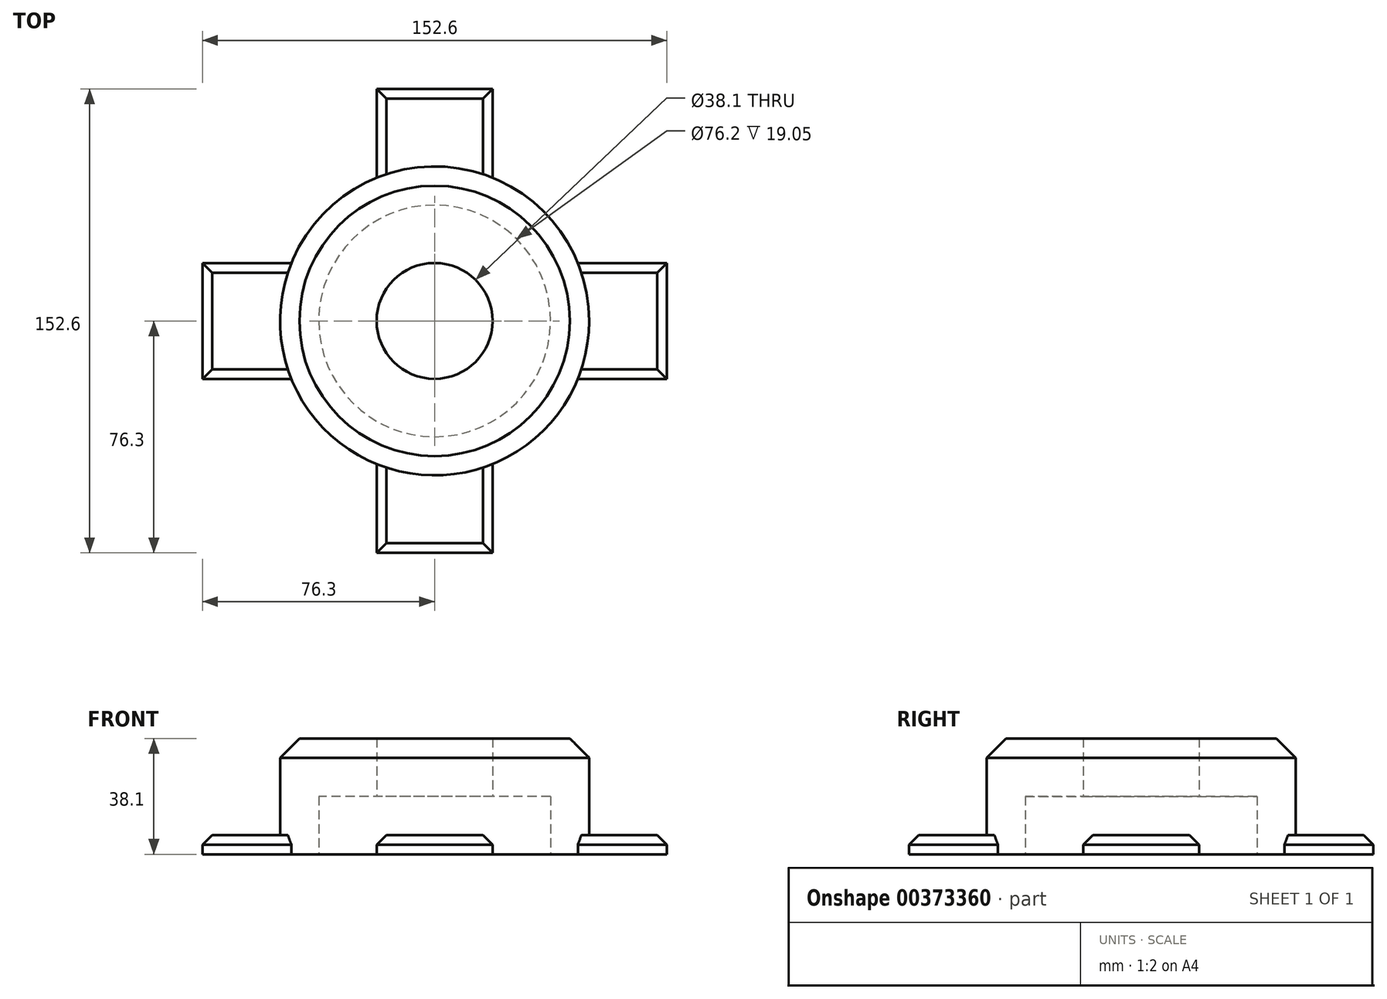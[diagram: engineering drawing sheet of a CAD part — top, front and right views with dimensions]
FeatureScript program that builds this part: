
annotation { "Feature Type Name" : "Feature", "Feature Type Description" : "" }
export const myFeature = defineFeature(function(context is Context, id is Id, definition is map)
    precondition{}
    {
        {
            var Q0;
            Q0=qCreatedBy(makeId("Top.planeOp"),FACE);
            var sketch = newSketch(context, id + "F0", { "sketchPlane" : qUnion([Q0])});
            skCircle(sketch, "E0", {"center": v(0, 0) * mm, "radius": 50.8 * mm});
            skLineSegment(sketch, "E1", {"start": v(0, 75.73) * mm, "end": v(0, -75.72) * mm, "construction": true});
            skLineSegment(sketch, "E2", {"start": v(-75.97, 0) * mm, "end": v(76.3, 0) * mm, "construction": true});
            skLineSegment(sketch, "E3", {"start": v(-19.05, 47.1) * mm, "end": v(-19.05, 76.3) * mm});
            skLineSegment(sketch, "E4", {"start": v(19.05, 47.1) * mm, "end": v(19.05, 76.3) * mm});
            skLineSegment(sketch, "E5", {"start": v(-47.1, 19.05) * mm, "end": v(-76.3, 19.05) * mm});
            skLineSegment(sketch, "E6", {"start": v(-47.1, -19.05) * mm, "end": v(-76.3, -19.05) * mm});
            skLineSegment(sketch, "E7", {"start": v(47.1, 19.05) * mm, "end": v(76.3, 19.05) * mm});
            skLineSegment(sketch, "E8", {"start": v(47.1, -19.05) * mm, "end": v(76.3, -19.05) * mm});
            skLineSegment(sketch, "E9", {"start": v(-19.05, -47.1) * mm, "end": v(-19.05, -76.3) * mm});
            skLineSegment(sketch, "E10", {"start": v(19.05, -47.1) * mm, "end": v(19.05, -76.3) * mm});
            skLineSegment(sketch, "E11", {"start": v(-76.3, 19.05) * mm, "end": v(-76.3, -19.05) * mm});
            skLineSegment(sketch, "E12", {"start": v(-19.05, 76.3) * mm, "end": v(19.05, 76.3) * mm});
            skLineSegment(sketch, "E13", {"start": v(76.3, 19.05) * mm, "end": v(76.3, -19.05) * mm});
            skLineSegment(sketch, "E14", {"start": v(19.05, -76.3) * mm, "end": v(-19.05, -76.3) * mm});
            skCircle(sketch, "E15", {"center": v(0, 0) * mm, "radius": 19.05 * mm});
            skSolve(sketch);
        }
        {
            var Q0;
            {var subQ0=sQuery(id+"F0.wireOp",EDGE,"E0");var subQ4=makeQuery(id+"F0.imprint","INTERSECT",VERTEX,{"derivedFrom":[subQ0,sQuery(id+"F0.wireOp",EDGE,"E4")]});Q0=makeQuery(id+"F0.imprint","IMPRINT",FACE,{"disambiguationData":[TD([[makeQuery(id+"F0.imprint","IMPRINT",EDGE,{"disambiguationData":[TD([[subQ4,1.0]])],"derivedFrom":subQ0}),1.0]])]});}
            extrude(context, id + "F1", {"entities" : qUnion([Q0]), "depth" : 38.1 * mm});
        }
        {
            var Q0;
            {var subQ0=sQuery(id+"F0.wireOp",EDGE,"E9");Q0=makeQuery(id+"F0.imprint","IMPRINT",FACE,{"disambiguationData":[TD([[makeQuery(id+"F0.imprint","IMPRINT",EDGE,{"derivedFrom":subQ0}),1.0]])]});}
            var Q1;
            {var subQ0=sQuery(id+"F0.wireOp",EDGE,"E5");Q1=makeQuery(id+"F0.imprint","IMPRINT",FACE,{"disambiguationData":[TD([[makeQuery(id+"F0.imprint","IMPRINT",EDGE,{"derivedFrom":subQ0}),1.0]])]});}
            var Q2;
            {var subQ0=sQuery(id+"F0.wireOp",EDGE,"E7");Q2=makeQuery(id+"F0.imprint","IMPRINT",FACE,{"disambiguationData":[TD([[makeQuery(id+"F0.imprint","IMPRINT",EDGE,{"derivedFrom":subQ0}),-1.0]])]});}
            var Q3;
            {var subQ0=sQuery(id+"F0.wireOp",EDGE,"E3");Q3=makeQuery(id+"F0.imprint","IMPRINT",FACE,{"disambiguationData":[TD([[makeQuery(id+"F0.imprint","IMPRINT",EDGE,{"derivedFrom":subQ0}),-1.0]])]});}
            extrude(context, id + "F2", {"entities" : qUnion([Q0, Q1, Q2, Q3]), "operationType" : NewBodyOperationType.ADD, "depth" : 6.35 * mm});
        }
        {
            var Q0;
            Q0=makeQuery(id+"F0.imprint","IMPRINT",FACE,{"disambiguationData":[TD([[makeQuery(id+"F0.imprint","IMPRINT",EDGE,{"derivedFrom":sQuery(id+"F0.wireOp",EDGE,"E15")}),-1.0]])]});
            var sketch = newSketch(context, id + "F3", { "sketchPlane" : qUnion([Q0])});
            skCircle(sketch, "E16", {"center": v(0, 0) * mm, "radius": 38.1 * mm});
            skSolve(sketch);
        }
        {
            var Q0;
            Q0 = qSketchRegion(id + "F3", true);
            extrude(context, id + "F4", {"entities" : qUnion([Q0]), "operationType" : NewBodyOperationType.REMOVE, "depth" : 19.05 * mm});
        }
        {
            var Q0;
            Q0=makeQuery(id+"F2.opExtrude","CAP_EDGE",EDGE,{"disambiguationData":[OSD([sQuery(id+"F0.wireOp",EDGE,"E14")])],"isStart":false});
            var Q1;
            Q1=makeQuery(id+"F2.opExtrude","CAP_EDGE",EDGE,{"disambiguationData":[OSD([sQuery(id+"F0.wireOp",EDGE,"E10")])],"isStart":false});
            var Q2;
            Q2=makeQuery(id+"F2.opExtrude","CAP_EDGE",EDGE,{"disambiguationData":[OSD([sQuery(id+"F0.wireOp",EDGE,"E9")])],"isStart":false});
            var Q3;
            Q3=makeQuery(id+"F2.opExtrude","CAP_EDGE",EDGE,{"disambiguationData":[OSD([sQuery(id+"F0.wireOp",EDGE,"E8")])],"isStart":false});
            var Q4;
            Q4=makeQuery(id+"F2.opExtrude","CAP_EDGE",EDGE,{"disambiguationData":[OSD([sQuery(id+"F0.wireOp",EDGE,"E13")])],"isStart":false});
            var Q5;
            Q5=makeQuery(id+"F2.opExtrude","CAP_EDGE",EDGE,{"disambiguationData":[OSD([sQuery(id+"F0.wireOp",EDGE,"E7")])],"isStart":false});
            var Q6;
            Q6=makeQuery(id+"F2.opExtrude","CAP_EDGE",EDGE,{"disambiguationData":[OSD([sQuery(id+"F0.wireOp",EDGE,"E5")])],"isStart":false});
            var Q7;
            Q7=makeQuery(id+"F2.opExtrude","CAP_EDGE",EDGE,{"disambiguationData":[OSD([sQuery(id+"F0.wireOp",EDGE,"E11")])],"isStart":false});
            var Q8;
            Q8=makeQuery(id+"F2.opExtrude","CAP_EDGE",EDGE,{"disambiguationData":[OSD([sQuery(id+"F0.wireOp",EDGE,"E6")])],"isStart":false});
            var Q9;
            Q9=makeQuery(id+"F2.opExtrude","CAP_EDGE",EDGE,{"disambiguationData":[OSD([sQuery(id+"F0.wireOp",EDGE,"E12")])],"isStart":false});
            var Q10;
            Q10=makeQuery(id+"F2.opExtrude","CAP_EDGE",EDGE,{"disambiguationData":[OSD([sQuery(id+"F0.wireOp",EDGE,"E4")])],"isStart":false});
            var Q11;
            Q11=makeQuery(id+"F2.opExtrude","CAP_EDGE",EDGE,{"disambiguationData":[OSD([sQuery(id+"F0.wireOp",EDGE,"E3")])],"isStart":false});
            chamfer(context, id + "F5", {"entities" : qUnion([Q0, Q1, Q2, Q3, Q4, Q5, Q6, Q7, Q8, Q9, Q10, Q11]), "width" : 3.17 * mm, "tangentPropagation" : true});
        }
        {
            var Q0;
            Q0=makeQuery(id+"F1.opExtrude","CAP_EDGE",EDGE,{"disambiguationData":[OSD([sQuery(id+"F0.wireOp",EDGE,"E0")])],"isStart":false});
            chamfer(context, id + "F6", {"entities" : qUnion([Q0]), "width" : 6.35 * mm, "tangentPropagation" : true});
        }
    });
